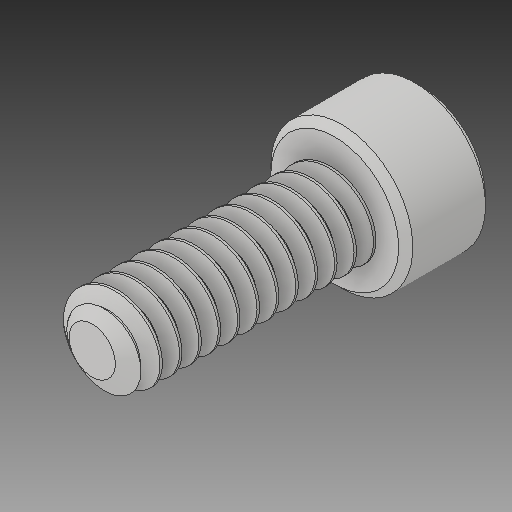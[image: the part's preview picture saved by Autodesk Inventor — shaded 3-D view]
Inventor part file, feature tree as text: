
AUTODESK INVENTOR PART (.ipt)
format: ipt  version: 2017 (Build 210142000, 142)  size: 783,360 bytes
history: native  units: in
note: dims shown in document units (in); Inventor stores cm internally (conversion verified against a paired STEP export)
features: chamfer x1
ambient origin geometry x8: Origin, YZ Plane, XZ Plane, XY Plane, X Axis, Y Axis, Z Axis, Center Point
bodies: Solid1 (feature_tree)
feature tree (1):
  chamfer  "Chamfer1"  [1 undecoded]
note: 1 required parameter value undecoded (feature->parameter linkage not recoverable at this tier; creation-order binding heuristic only, values carry confidence <= 0.55)
